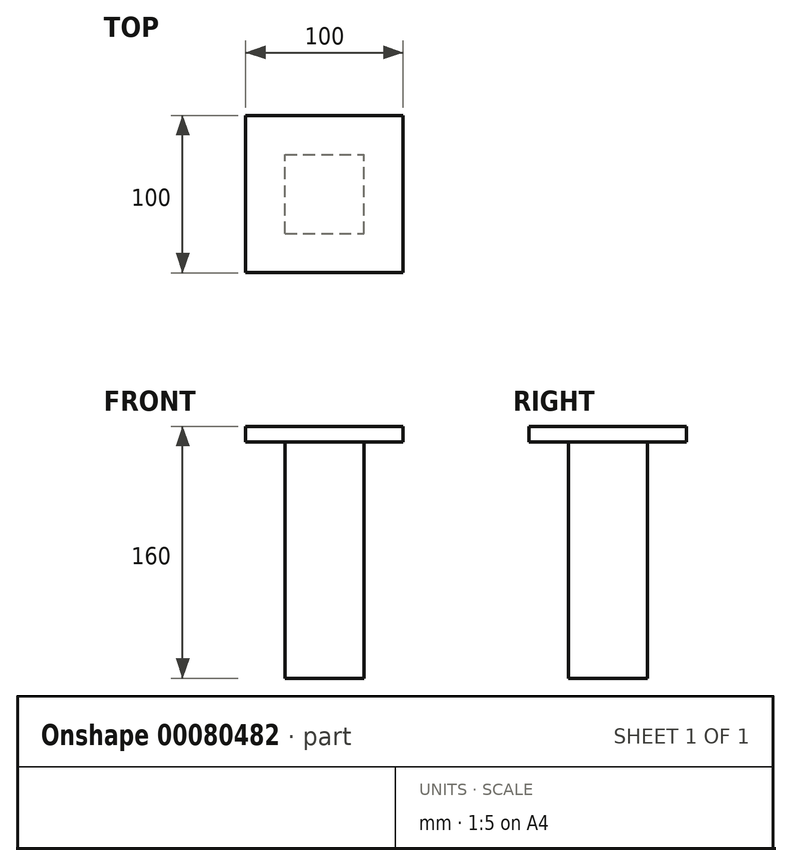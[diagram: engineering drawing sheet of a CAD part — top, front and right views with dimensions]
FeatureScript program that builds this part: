
annotation { "Feature Type Name" : "Feature", "Feature Type Description" : "" }
export const myFeature = defineFeature(function(context is Context, id is Id, definition is map)
    precondition{}
    {
        {
            var Q0;
            Q0=qCreatedBy(makeId("Top.planeOp"),FACE);
            var sketch = newSketch(context, id + "F0", { "sketchPlane" : qUnion([Q0])});
            skLineSegment(sketch, "E0.bottom", {"start": v(-23.16, -26.67) * mm, "end": v(26.84, -26.67) * mm});
            skLineSegment(sketch, "E0.top", {"start": v(-23.16, 23.33) * mm, "end": v(26.84, 23.33) * mm});
            skLineSegment(sketch, "E0.left", {"start": v(-23.16, -26.67) * mm, "end": v(-23.16, 23.33) * mm});
            skLineSegment(sketch, "E0.right", {"start": v(26.84, -26.67) * mm, "end": v(26.84, 23.33) * mm});
            skSolve(sketch);
        }
        {
            var Q0;
            Q0=makeQuery(id+"F0.imprint","IMPRINT",FACE,{"disambiguationData":[TD([[makeQuery(id+"F0.imprint","IMPRINT",EDGE,{"derivedFrom":sQuery(id+"F0.wireOp",EDGE,"E0.bottom")}),1.0]])]});
            extrude(context, id + "F1", {"entities" : qUnion([Q0]), "depth" : 150 * mm});
        }
        {
            var Q0;
            Q0=makeQuery(id+"F1.opExtrude","CAP_FACE",FACE,{"disambiguationData":[OSD([sQuery(id+"F0.wireOp",EDGE,"E0.bottom"),sQuery(id+"F0.wireOp",EDGE,"E0.top"),sQuery(id+"F0.wireOp",EDGE,"E0.left"),sQuery(id+"F0.wireOp",EDGE,"E0.right")])],"isStart":false});
            var sketch = newSketch(context, id + "F2", { "sketchPlane" : qUnion([Q0])});
            skLineSegment(sketch, "E1.bottom", {"start": v(51.84, 48.33) * mm, "end": v(-48.16, 48.33) * mm});
            skLineSegment(sketch, "E1.top", {"start": v(51.84, -51.67) * mm, "end": v(-48.16, -51.67) * mm});
            skLineSegment(sketch, "E1.left", {"start": v(51.84, 48.33) * mm, "end": v(51.84, -51.67) * mm});
            skLineSegment(sketch, "E1.right", {"start": v(-48.16, 48.33) * mm, "end": v(-48.16, -51.67) * mm});
            skLineSegment(sketch, "E2.0", {"start": v(41.84, 38.33) * mm, "end": v(41.84, -41.67) * mm});
            skLineSegment(sketch, "E3.0", {"start": v(51.84, 58.33) * mm, "end": v(-48.16, 58.33) * mm});
            skLineSegment(sketch, "E4.0", {"start": v(41.84, 38.33) * mm, "end": v(-38.16, 38.33) * mm});
            skLineSegment(sketch, "E4.1", {"start": v(-38.16, 38.33) * mm, "end": v(-38.16, -41.67) * mm});
            skLineSegment(sketch, "E4.2", {"start": v(41.84, -41.67) * mm, "end": v(-38.16, -41.67) * mm});
            skSolve(sketch);
        }
        {
            var Q0;
            Q0 = qSketchRegion(id + "F2", true);
            var Q1;
            Q1=makeQuery(id+"F2.imprint","IMPRINT",FACE,{"disambiguationData":[TD([[makeQuery(id+"F2.imprint","IMPRINT",EDGE,{"derivedFrom":makeQuery(id+"F1.opExtrude","CAP_EDGE",EDGE,{"disambiguationData":[OSD([sQuery(id+"F0.wireOp",EDGE,"E0.bottom")])],"isStart":false})}),1.0]])]});
            var Q2;
            Q2=makeQuery(id+"F2.imprint","IMPRINT",FACE,{"disambiguationData":[TD([[makeQuery(id+"F2.imprint","IMPRINT",EDGE,{"derivedFrom":sQuery(id+"F2.wireOp",EDGE,"E2.0")}),-1.0]])]});
            extrude(context, id + "F3", {"entities" : qUnion([Q0, Q1, Q2]), "operationType" : NewBodyOperationType.ADD, "depth" : 10 * mm});
        }
    });
